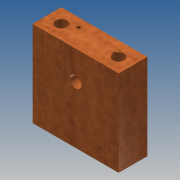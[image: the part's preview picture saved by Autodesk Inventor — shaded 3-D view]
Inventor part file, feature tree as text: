
AUTODESK INVENTOR PART (.ipt)
format: ipt  version: 2014 SP1 (Build 180222100, 222)  size: 108,544 bytes
history: native  units: in
note: dims shown in document units (in); Inventor stores cm internally (conversion verified against a paired STEP export)
features: sketch x3, hole x2, extrude x1
ambient origin geometry x8: Origin, YZ Plane, XZ Plane, XY Plane, X Axis, Y Axis, Z Axis, Center Point
bodies: Solid1 (feature_tree)
feature tree (6):
  extrude  "Extrusion1"  Depth=0.5in
  hole  "Hole1"  [1 undecoded]
  hole  "Hole2"  [1 undecoded]
  sketch  "Sketch1"  dims[d0=1.5in d1=0.5in]
  sketch  "Sketch2"  dims[d2=1.5in d3=0.0in d4=0.5in]
  sketch  "Sketch3"  dims[d5=0.201in d6=0.75in d7=0.385in d8=0.25in d9=0.5635in d10=1.0in d11=0.8108in d12=0.5in d13=0.201in d14=0.75in d15=0.385in d16=0.25in d17=0.5635in d18=1.0in d19=0.8108in]
note: 2 required parameter values undecoded (feature->parameter linkage not recoverable at this tier; creation-order binding heuristic only, values carry confidence <= 0.55)
